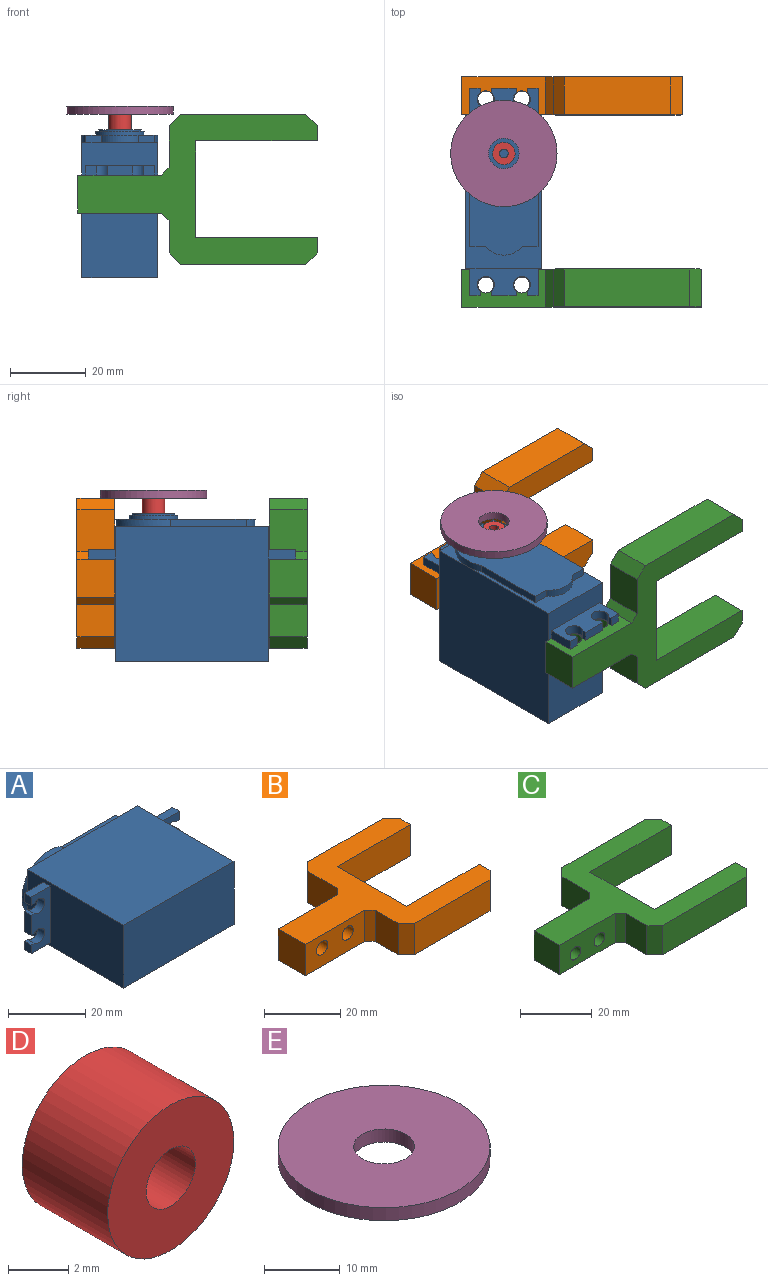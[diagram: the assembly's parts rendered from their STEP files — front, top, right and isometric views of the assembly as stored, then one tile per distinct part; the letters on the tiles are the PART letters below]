
ASSEMBLY  parts=5 mates=4
PART A: 44 faces, bbox 54.5x39x20 mm
  f0: plane 35.5x20mm, normal (-1,0,0), area 665mm2, adj f5,f6,f7,f8,f31,f32,f33,f39
  f1: plane 35.5x20mm, normal (1,0,0), area 665mm2, adj f4,f6,f7,f8,f18,f24,f25,f38
  f2: plane 12.8x12.8mm, normal (0,1,0), area 31mm2, adj f15,f16
  f3: plane 36.76x20mm, normal (0,1,0), area 488.8mm2, adj f9,f10,f11,f12,f13,f14,f15
  f4: plane 30.36x20mm, normal (0,1,0), area 146.7mm2, adj f1,f6,f7,f9,f10,f11,f12,f13
  f5: plane 20x10.14mm, normal (0,1,0), area 45.7mm2, adj f0,f6,f7,f9
  f6: plane 40.5x35.5mm, normal (0,0,1), area 1437.8mm2, adj f0,f1,f4,f5,f8
  f7: plane 40.5x35.5mm, normal (0,0,-1), area 1437.8mm2, adj f0,f1,f4,f5,f8
  f8: plane 40.5x20mm, normal (0,-1,0), area 810mm2, adj f0,f1,f6,f7
  f9: cylinder r=10mm len=20mm, axis (0,-1,0), area 80.9mm2, adj f3,f4,f5,f10,f14
  f10: plane 20x2mm, normal (0,0,1), area 40mm2, adj f3,f4,f9,f11
  f11: plane 4.2x2mm, normal (1,0,0), area 8.4mm2, adj f3,f4,f10,f12
  f12: cylinder r=6mm len=9.6mm, axis (0,-1,0), area 22.3mm2, adj f3,f4,f11,f13
  f13: plane 4.2x2mm, normal (1,0,0), area 8.4mm2, adj f3,f4,f12,f14
  f14: plane 20x2mm, normal (0,0,-1), area 40mm2, adj f3,f4,f9,f13
  f15: cylinder r=6.4mm len=12.8mm, axis (0,-1,0), area 40.2mm2, adj f2,f3
  f16: cylinder r=5.58mm len=11.15mm, axis (0,-1,0), area 17.5mm2, adj f2,f17
  f17: plane 11.15x11.15mm, normal (0,1,0), area 97.6mm2, adj f16
  f18: plane 7x2.5mm, normal (0,0,-1), area 17.5mm2, adj f1,f19,f24,f25
  f19: plane 2.75x2.5mm, normal (1,0,0), area 6.9mm2, adj f18,f20,f24,f25
  f20: plane 2.5x1.07mm, normal (0,0,1), area 2.7mm2, adj f19,f21,f24,f25
  f21: cylinder r=2.25mm len=4.5mm, axis (0,1,0), area 27.1mm2, adj f20,f22,f24,f25
  f22: plane 2.5x1.07mm, normal (0,0,-1), area 2.7mm2, adj f21,f23,f24,f25
  f23: plane 6.5x2.5mm, normal (1,0,0), area 16.2mm2, adj f22,f24,f25,f34
  f24: plane 18x7mm, normal (0,-1,0), area 90.1mm2, adj f1,f18,f19,f20,f21,f22,f23,f34
  f25: plane 18x7mm, normal (0,1,0), area 90.1mm2, adj f1,f18,f19,f20,f21,f22,f23,f34
  f26: plane 6.5x2.5mm, normal (-1,0,0), area 16.2mm2, adj f27,f32,f33,f43
  f27: plane 2.5x1.07mm, normal (0,0,-1), area 2.7mm2, adj f26,f28,f32,f33
  f28: cylinder r=2.25mm len=4.5mm, axis (0,1,0), area 27.1mm2, adj f27,f29,f32,f33
  f29: plane 2.5x1.07mm, normal (0,0,1), area 2.7mm2, adj f28,f30,f32,f33
  f30: plane 2.75x2.5mm, normal (-1,0,0), area 6.9mm2, adj f29,f31,f32,f33
  f31: plane 7x2.5mm, normal (0,0,-1), area 17.5mm2, adj f0,f30,f32,f33
  f32: plane 18x7mm, normal (0,-1,0), area 90.1mm2, adj f0,f26,f27,f28,f29,f30,f31,f39
  f33: plane 18x7mm, normal (0,1,0), area 90.1mm2, adj f0,f26,f27,f28,f29,f30,f31,f39
  f34: plane 2.5x1.07mm, normal (0,0,1), area 2.7mm2, adj f23,f24,f25,f35
  f35: cylinder r=2.25mm len=4.5mm, axis (0,1,0), area 27.1mm2, adj f24,f25,f34,f36
  f36: plane 2.5x1.07mm, normal (0,0,-1), area 2.7mm2, adj f24,f25,f35,f37
  f37: plane 2.75x2.5mm, normal (1,0,0), area 6.9mm2, adj f24,f25,f36,f38
  f38: plane 7x2.5mm, normal (0,0,1), area 17.5mm2, adj f1,f24,f25,f37
  f39: plane 7x2.5mm, normal (0,0,1), area 17.5mm2, adj f0,f32,f33,f40
  f40: plane 2.75x2.5mm, normal (-1,0,0), area 6.9mm2, adj f32,f33,f39,f41
  f41: plane 2.5x1.07mm, normal (0,0,-1), area 2.7mm2, adj f32,f33,f40,f42
  f42: cylinder r=2.25mm len=4.5mm, axis (0,1,0), area 27.1mm2, adj f32,f33,f41,f43
  f43: plane 2.5x1.07mm, normal (0,0,1), area 2.7mm2, adj f26,f32,f33,f42
PART B: 22 faces, bbox 58x39.5x10 mm
  f0: plane 10x2mm, normal (-0.71,-0.71,0), area 28.3mm2, adj f1,f13,f14,f15
  f1: plane 10x8.5mm, normal (-1,0,0), area 85mm2, adj f0,f14,f15,f20
  f2: plane 28x10mm, normal (0,-1,0), area 280mm2, adj f14,f15,f20,f21
  f3: plane 10x4mm, normal (1,0,0), area 40mm2, adj f4,f14,f15,f21
  f4: plane 27x10mm, normal (0,1,0), area 270mm2, adj f3,f5,f14,f15
  f5: plane 25.5x10mm, normal (1,0,0), area 255mm2, adj f4,f6,f14,f15
  f6: plane 27x10mm, normal (0,-1,0), area 270mm2, adj f5,f7,f14,f15
  f7: plane 10x4mm, normal (1,0,0), area 40mm2, adj f6,f14,f15,f19
  f8: plane 28x10mm, normal (0,1,0), area 280mm2, adj f14,f15,f18,f19
  f9: plane 11x10mm, normal (-1,0,0), area 110mm2, adj f10,f14,f15,f18
  f10: plane 10x2mm, normal (-0.71,0.71,0), area 28.3mm2, adj f9,f11,f14,f15
  f11: plane 22x10mm, normal (0,1,0), area 192.3mm2, adj f10,f12,f14,f15,f16,f17
  f12: plane 10x10mm, normal (-1,0,0), area 100mm2, adj f11,f13,f14,f15
  f13: plane 22x10mm, normal (0,-1,0), area 192.3mm2, adj f0,f12,f14,f15,f16,f17
  f14: plane 58x39.5mm, normal (0,0,1), area 880.5mm2, adj f0,f1,f2,f3,f4,f5,f6,f7
  f15: plane 58x39.5mm, normal (0,0,-1), area 880.5mm2, adj f0,f1,f2,f3,f4,f5,f6,f7
  f16: cylinder r=2.1mm len=10mm, axis (0,-1,0), area 131.9mm2, adj f11,f13
  f17: cylinder r=2.1mm len=10mm, axis (0,-1,0), area 131.9mm2, adj f11,f13
  f18: plane 10x3mm, normal (-0.71,0.71,0), area 42.4mm2, adj f8,f9,f14,f15
  f19: plane 10x3mm, normal (0.71,0.71,0), area 42.4mm2, adj f7,f8,f14,f15
  f20: plane 10x3mm, normal (-0.71,-0.71,0), area 42.4mm2, adj f1,f2,f14,f15
  f21: plane 10x3mm, normal (0.71,-0.71,0), area 42.4mm2, adj f2,f3,f14,f15
PART C: 22 faces, bbox 63x39.5x10 mm
  f0: plane 10x2mm, normal (-0.71,-0.71,0), area 28.3mm2, adj f1,f13,f14,f15
  f1: plane 10x8.5mm, normal (-1,0,0), area 85mm2, adj f0,f14,f15,f20
  f2: plane 33x10mm, normal (0,-1,0), area 330mm2, adj f14,f15,f20,f21
  f3: plane 10x4mm, normal (1,0,0), area 40mm2, adj f4,f14,f15,f21
  f4: plane 32x10mm, normal (0,1,0), area 320mm2, adj f3,f5,f14,f15
  f5: plane 25.5x10mm, normal (1,0,0), area 255mm2, adj f4,f6,f14,f15
  f6: plane 32x10mm, normal (0,-1,0), area 320mm2, adj f5,f7,f14,f15
  f7: plane 10x4mm, normal (1,0,0), area 40mm2, adj f6,f14,f15,f19
  f8: plane 33x10mm, normal (0,1,0), area 330mm2, adj f14,f15,f18,f19
  f9: plane 11x10mm, normal (-1,0,0), area 110mm2, adj f10,f14,f15,f18
  f10: plane 10x2mm, normal (-0.71,0.71,0), area 28.3mm2, adj f9,f11,f14,f15
  f11: plane 22x10mm, normal (0,1,0), area 192.3mm2, adj f10,f12,f14,f15,f16,f17
  f12: plane 10x10mm, normal (-1,0,0), area 100mm2, adj f11,f13,f14,f15
  f13: plane 22x10mm, normal (0,-1,0), area 192.3mm2, adj f0,f12,f14,f15,f16,f17
  f14: plane 63x39.5mm, normal (0,0,1), area 950.5mm2, adj f0,f1,f2,f3,f4,f5,f6,f7
  f15: plane 63x39.5mm, normal (0,0,-1), area 950.5mm2, adj f0,f1,f2,f3,f4,f5,f6,f7
  f16: cylinder r=2.1mm len=10mm, axis (0,-1,0), area 131.9mm2, adj f11,f13
  f17: cylinder r=2.1mm len=10mm, axis (0,-1,0), area 131.9mm2, adj f11,f13
  f18: plane 10x3mm, normal (-0.71,0.71,0), area 42.4mm2, adj f8,f9,f14,f15
  f19: plane 10x3mm, normal (0.71,0.71,0), area 42.4mm2, adj f7,f8,f14,f15
  f20: plane 10x3mm, normal (-0.71,-0.71,0), area 42.4mm2, adj f1,f2,f14,f15
  f21: plane 10x3mm, normal (0.71,-0.71,0), area 42.4mm2, adj f2,f3,f14,f15
PART D: 4 faces, bbox 5.9x4x5.9 mm
  f0: plane 5.9x5.9mm, normal (0,1,0), area 23.2mm2, adj f2,f3
  f1: plane 5.9x5.9mm, normal (0,-1,0), area 23.2mm2, adj f2,f3
  f2: cylinder r=2.95mm len=5.9mm, axis (0,-1,0), area 74.1mm2, adj f0,f1
  f3: cylinder r=1.15mm len=4mm, axis (0,-1,0), area 28.9mm2, adj f0,f1
PART E: 4 faces, bbox 28x28x2.1 mm
  f0: cylinder r=4mm len=8mm, axis (0,0,-1), area 52.8mm2, adj f2,f3
  f1: cylinder r=14mm len=28mm, axis (0,0,-1), area 184.7mm2, adj f2,f3
  f2: plane 28x28mm, normal (0,0,1), area 565.5mm2, adj f0,f1
  f3: plane 28x28mm, normal (0,0,-1), area 565.5mm2, adj f0,f1
PLACE A rot(axis=(0.58,-0.58,-0.58),120deg) t=(-91.65,28.51,-11.63)mm
PLACE B rot(axis=(1,0,0),90deg) t=(-58.2,58.81,11.62)mm
PLACE C rot(axis=(1,0,0),90deg) t=(-55.7,8.21,11.62)mm fixed
PLACE D rot(axis=(1,0,0),90deg) t=(-91.65,38.62,27.37)mm
PLACE E t=(-91.65,38.62,6.37)mm
MATE fastened B.f17 <-> A.f42  axis (0,0,1) through (-96.4,53.01,15.37)mm
MATE fastened D.f2 <-> A.f9  axis (0,0,-1) through (-91.65,38.62,27.37)mm
MATE fastened D.f2 <-> E.f1  axis (0,0,1) through (-91.65,38.62,31.37)mm
MATE fastened C.f17 <-> A.f35  axis (0,0,1) through (-96.4,4.01,15.37)mm
